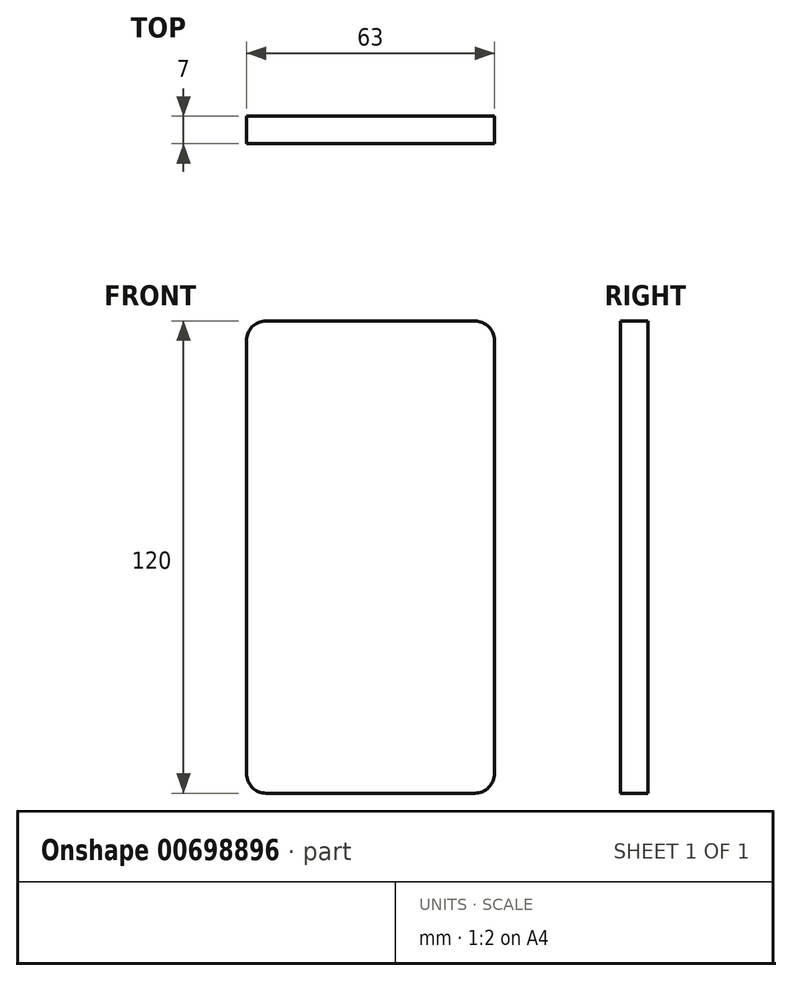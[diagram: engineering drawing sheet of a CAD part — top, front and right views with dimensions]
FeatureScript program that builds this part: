
annotation { "Feature Type Name" : "Feature", "Feature Type Description" : "" }
export const myFeature = defineFeature(function(context is Context, id is Id, definition is map)
    precondition{}
    {
        {
            var Q0;
            Q0=qCreatedBy(makeId("Front.planeOp"),FACE);
            var sketch = newSketch(context, id + "F0", { "sketchPlane" : qUnion([Q0])});
            skLineSegment(sketch, "E0.bottom", {"start": v(0, 0) * mm, "end": v(-63, 0) * mm});
            skLineSegment(sketch, "E0.top", {"start": v(0, 120) * mm, "end": v(-63, 120) * mm});
            skLineSegment(sketch, "E0.left", {"start": v(0, 0) * mm, "end": v(0, 120) * mm});
            skLineSegment(sketch, "E0.right", {"start": v(-63, 0) * mm, "end": v(-63, 120) * mm});
            skSolve(sketch);
        }
        {
            var Q0;
            Q0 = qSketchRegion(id + "F0", true);
            extrude(context, id + "F1", {"entities" : qUnion([Q0]), "depth" : 7 * mm, "offsetDistance" : 25 * mm});
        }
        {
            var Q0;
            Q0=makeQuery(id+"F1.opExtrude","SWEPT_EDGE",EDGE,{"disambiguationData":[OSD([sQuery(id+"F0.wireOp",EDGE,"E0.top"),sQuery(id+"F0.wireOp",EDGE,"E0.right")])]});
            fillet(context, id + "F2", {"entities" : qUnion([Q0]), "radius" : 5 * mm, "tangentPropagation" : true, "allowEdgeOverflow" : false});
        }
        {
            var Q0;
            Q0=makeQuery(id+"F1.opExtrude","SWEPT_EDGE",EDGE,{"disambiguationData":[OSD([sQuery(id+"F0.wireOp",EDGE,"E0.top"),sQuery(id+"F0.wireOp",EDGE,"E0.left")])]});
            var Q1;
            Q1=makeQuery(id+"F1.opExtrude","SWEPT_EDGE",EDGE,{"disambiguationData":[OSD([sQuery(id+"F0.wireOp",EDGE,"E0.bottom"),sQuery(id+"F0.wireOp",EDGE,"E0.right")])]});
            var Q2;
            Q2=makeQuery(id+"F1.opExtrude","SWEPT_EDGE",EDGE,{"disambiguationData":[OSD([sQuery(id+"F0.wireOp",EDGE,"E0.bottom"),sQuery(id+"F0.wireOp",EDGE,"E0.left")])]});
            fillet(context, id + "F3", {"entities" : qUnion([Q0, Q1, Q2]), "radius" : 5 * mm, "tangentPropagation" : true, "allowEdgeOverflow" : false});
        }
    });
